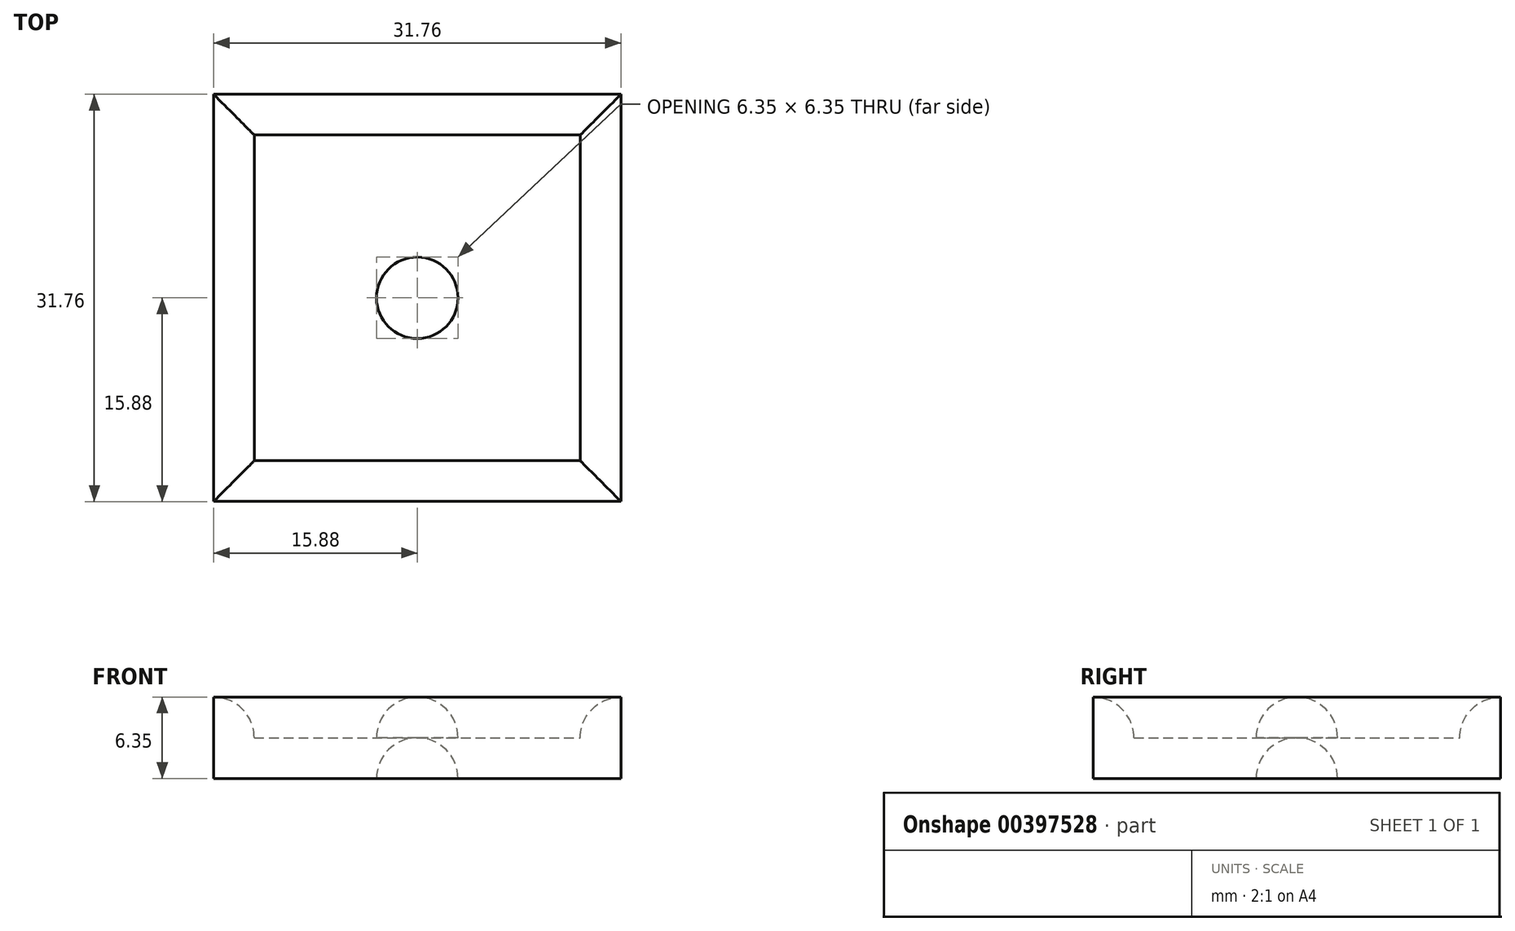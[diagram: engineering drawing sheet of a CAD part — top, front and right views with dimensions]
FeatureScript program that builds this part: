
annotation { "Feature Type Name" : "Feature", "Feature Type Description" : "" }
export const myFeature = defineFeature(function(context is Context, id is Id, definition is map)
    precondition{}
    {
        {
            var Q0;
            Q0=qCreatedBy(makeId("Top.planeOp"),FACE);
            var sketch = newSketch(context, id + "F0", { "sketchPlane" : qUnion([Q0])});
            skLineSegment(sketch, "E0.bottom", {"start": v(12.7, 12.7) * mm, "end": v(-12.7, 12.7) * mm});
            skLineSegment(sketch, "E0.top", {"start": v(12.7, -12.7) * mm, "end": v(-12.7, -12.7) * mm});
            skLineSegment(sketch, "E0.left", {"start": v(12.7, 12.7) * mm, "end": v(12.7, -12.7) * mm});
            skLineSegment(sketch, "E0.right", {"start": v(-12.7, 12.7) * mm, "end": v(-12.7, -12.7) * mm});
            skPoint(sketch, "E0.middle", {"position": v(0, 0) * mm});
            skLineSegment(sketch, "E1.bottom", {"start": v(15.87, 15.88) * mm, "end": v(-15.88, 15.87) * mm});
            skLineSegment(sketch, "E1.top", {"start": v(15.88, -15.87) * mm, "end": v(-15.87, -15.88) * mm});
            skLineSegment(sketch, "E1.left", {"start": v(15.88, 15.88) * mm, "end": v(15.88, -15.87) * mm});
            skLineSegment(sketch, "E1.right", {"start": v(-15.88, 15.87) * mm, "end": v(-15.88, -15.88) * mm});
            skCircle(sketch, "E2", {"center": v(0, 0) * mm, "radius": 3.18 * mm});
            skLineSegment(sketch, "E3", {"start": v(0, -3.18) * mm, "end": v(0, 3.18) * mm});
            skSolve(sketch);
        }
        {
            var Q0;
            Q0=makeQuery(id+"F0.imprint","IMPRINT",FACE,{"disambiguationData":[TD([[makeQuery(id+"F0.imprint","IMPRINT",EDGE,{"derivedFrom":sQuery(id+"F0.wireOp",EDGE,"E0.bottom")}),-1.0]])]});
            var Q1;
            Q1=makeQuery(id+"F0.imprint","IMPRINT",FACE,{"disambiguationData":[TD([[makeQuery(id+"F0.imprint","IMPRINT",EDGE,{"derivedFrom":sQuery(id+"F0.wireOp",EDGE,"E0.bottom")}),1.0]])]});
            var Q2;
            {var subQ0=sQuery(id+"F0.wireOp",EDGE,"E3");Q2=makeQuery(id+"F0.imprint","IMPRINT",FACE,{"disambiguationData":[TD([[makeQuery(id+"F0.imprint","IMPRINT",EDGE,{"derivedFrom":subQ0}),-1.0]])]});}
            var Q3;
            {var subQ0=sQuery(id+"F0.wireOp",EDGE,"E3");Q3=makeQuery(id+"F0.imprint","IMPRINT",FACE,{"disambiguationData":[TD([[makeQuery(id+"F0.imprint","IMPRINT",EDGE,{"derivedFrom":subQ0}),1.0]])]});}
            extrude(context, id + "F1", {"entities" : qUnion([Q0, Q1, Q2, Q3]), "depth" : 3.17 * mm});
        }
        {
            var Q0;
            Q0=makeQuery(id+"F0.imprint","IMPRINT",FACE,{"disambiguationData":[TD([[makeQuery(id+"F0.imprint","IMPRINT",EDGE,{"derivedFrom":sQuery(id+"F0.wireOp",EDGE,"E0.bottom")}),-1.0]])]});
            extrude(context, id + "F2", {"entities" : qUnion([Q0]), "operationType" : NewBodyOperationType.ADD, "depth" : 6.35 * mm});
        }
        {
            var Q0;
            Q0=makeQuery(id+"F1.opExtrude","CAP_FACE",FACE,{"disambiguationData":[OSD([sQuery(id+"F0.wireOp",EDGE,"E1.bottom"),sQuery(id+"F0.wireOp",EDGE,"E1.top"),sQuery(id+"F0.wireOp",EDGE,"E1.left"),sQuery(id+"F0.wireOp",EDGE,"E1.right")])],"isStart":false});
            var sketch = newSketch(context, id + "F3", { "sketchPlane" : qUnion([Q0])});
            skCircle(sketch, "E4.0", {"center": v(0, 0) * mm, "radius": 3.18 * mm});
            skLineSegment(sketch, "E4.1", {"start": v(0, -3.18) * mm, "end": v(0, 3.18) * mm});
            skSolve(sketch);
        }
        {
            var Q0;
            {var subQ0=sQuery(id+"F3.wireOp",EDGE,"E4.1");Q0=makeQuery(id+"F3.imprint","IMPRINT",FACE,{"disambiguationData":[TD([[makeQuery(id+"F3.imprint","IMPRINT",EDGE,{"derivedFrom":subQ0}),1.0]])]});}
            var Q1;
            Q1=sQuery(id+"F3.wireOp",EDGE,"E4.1");
            revolve(context, id + "F4", {"operationType" : NewBodyOperationType.ADD, "entities" : qUnion([Q0]), "axis" : qUnion([Q1]), "revolveType" : RevolveType.FULL});
        }
        {
            var Q0;
            {var subQ0=sQuery(id+"F0.wireOp",EDGE,"E3");Q0=makeQuery(id+"F0.imprint","IMPRINT",FACE,{"disambiguationData":[TD([[makeQuery(id+"F0.imprint","IMPRINT",EDGE,{"derivedFrom":subQ0}),1.0]])]});}
            var Q1;
            Q1=sQuery(id+"F0.wireOp",EDGE,"E3");
            revolve(context, id + "F5", {"operationType" : NewBodyOperationType.REMOVE, "entities" : qUnion([Q0]), "axis" : qUnion([Q1]), "revolveType" : RevolveType.FULL, "oppositeDirection" : true});
        }
        {
            var Q0;
            Q0=makeQuery(id+"F2.opExtrude","CAP_EDGE",EDGE,{"disambiguationData":[OSD([sQuery(id+"F0.wireOp",EDGE,"E0.bottom")])],"isStart":false});
            var Q1;
            Q1=makeQuery(id+"F2.opExtrude","CAP_EDGE",EDGE,{"disambiguationData":[OSD([sQuery(id+"F0.wireOp",EDGE,"E0.left")])],"isStart":false});
            var Q2;
            Q2=makeQuery(id+"F2.opExtrude","CAP_EDGE",EDGE,{"disambiguationData":[OSD([sQuery(id+"F0.wireOp",EDGE,"E0.right")])],"isStart":false});
            var Q3;
            Q3=makeQuery(id+"F2.opExtrude","CAP_EDGE",EDGE,{"disambiguationData":[OSD([sQuery(id+"F0.wireOp",EDGE,"E0.top")])],"isStart":false});
            fillet(context, id + "F6", {"entities" : qUnion([Q0, Q1, Q2, Q3]), "radius" : 3.17 * mm, "tangentPropagation" : true, "allowEdgeOverflow" : false});
        }
    });
